SOLIDWORKS PART (.sldprt)
format: sldprt  version: not decoded by parser v0  size: 282,624 bytes
history: native  units: mm
features: sketch x10, plane x9, cut_extrude x7, shell x3, material x1, extrude x1 (+13 scaffold rows collapsed)
feature tree (44):
  scaffold x13  (default folders/planes/origin — collapsed)
  material  "材质 <未指定>"
  plane  "前视基准面"
  plane  "上视基准面"
  plane  "右视基准面"
  plane  "基准面1"  Offset=1475mm
  plane  "基准面2"  Offset=1475mm
  sketch  "草图2"  dims[D1=200.0mm]
  sketch  "草图3"  dims[D1=200.0mm]
  sketch  "草图4"  dims[D1=100.0mm]
  cut_extrude  "切除-拉伸1"  Depth=100mm
  plane  "基准面3"  Offset=625mm
  plane  "基准面4"  Offset=625mm
  sketch  "草图5"  dims[D1=100.0mm]
  cut_extrude  "切除-拉伸3"  Depth=100mm
  sketch  "草图6"  dims[D1=100.0mm]
  cut_extrude  "切除-拉伸4"  Depth=100mm
  plane  "基准面5"  Offset=400mm
  sketch  "草图7"  dims[D1=100.0mm]
  cut_extrude  "切除-拉伸5"  Depth=100mm
  plane  "基准面6"  Offset=300mm
  sketch  "草图8"
  cut_extrude  "切除-拉伸6"  Depth=300mm
  sketch  "草图9"  dims[D1=150.0mm]
  cut_extrude  "切除-拉伸7"  Depth=50mm
  sketch  "草图10"
  cut_extrude  "切除-拉伸8"  Depth=200mm
  sketch  "草图11"  dims[c1.D2=60.0mm c1.D3=60.0mm c1.D4=80.0mm c2.D2=~180.613742mm c2.D3=~31.407628mm c2.D1=0.0mm]
  extrude  "凸台-拉伸1"  Depth=40mm
  shell  "抽壳1"  Thickness=2mm
  shell  "抽壳2"  Thickness=2mm
  shell  "抽壳3"  Thickness=2mm
decode coverage: 19 of 21 modeling features carry decoded parameters
note: ~ marks probable driven/reference dimensions
note: suppression state not decoded; provenance and decode notes live in map.json
